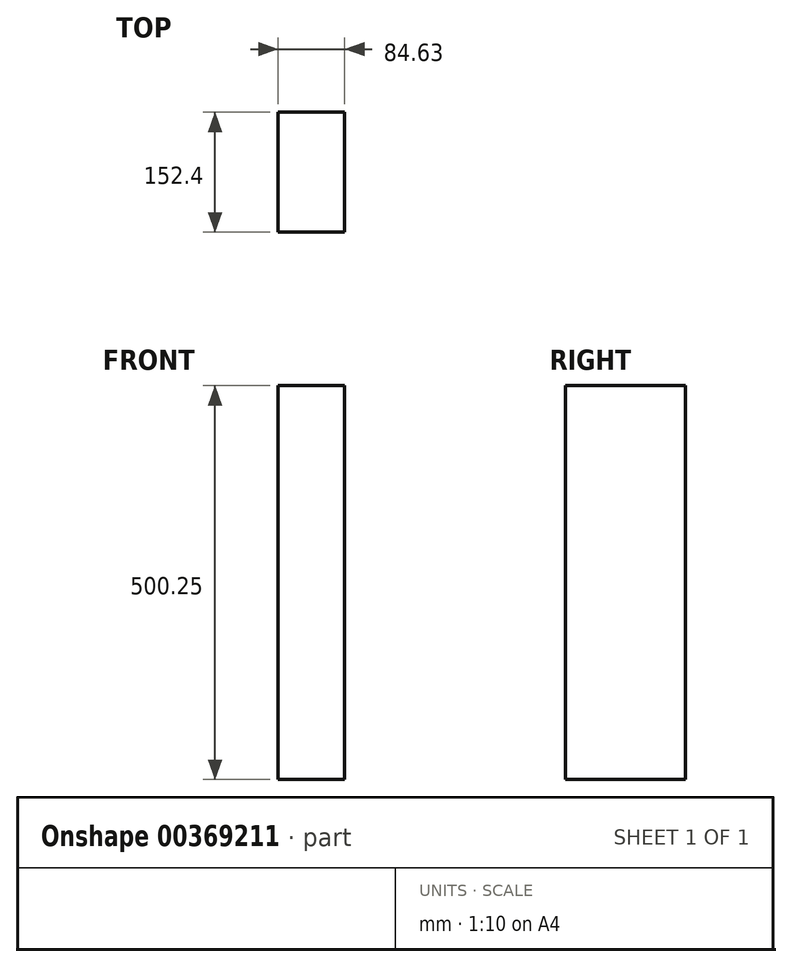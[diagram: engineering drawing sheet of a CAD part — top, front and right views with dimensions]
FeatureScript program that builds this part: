
annotation { "Feature Type Name" : "Feature", "Feature Type Description" : "" }
export const myFeature = defineFeature(function(context is Context, id is Id, definition is map)
    precondition{}
    {
        {
            var Q0;
            Q0=qCreatedBy(makeId("Front.planeOp"),FACE);
            var sketch = newSketch(context, id + "F0", { "sketchPlane" : qUnion([Q0])});
            skLineSegment(sketch, "E0.bottom", {"start": v(-136.84, 183.3) * mm, "end": v(-52.2, 183.3) * mm});
            skLineSegment(sketch, "E0.top", {"start": v(-136.84, -316.95) * mm, "end": v(-52.2, -316.95) * mm});
            skLineSegment(sketch, "E0.left", {"start": v(-136.84, 183.3) * mm, "end": v(-136.84, -316.95) * mm});
            skLineSegment(sketch, "E0.right", {"start": v(-52.2, 183.3) * mm, "end": v(-52.2, -316.95) * mm});
            skSolve(sketch);
        }
        {
            var Q0;
            Q0 = qSketchRegion(id + "F0", true);
            extrude(context, id + "F1", {"entities" : qUnion([Q0]), "depth" : 152.4 * mm});
        }
    });
